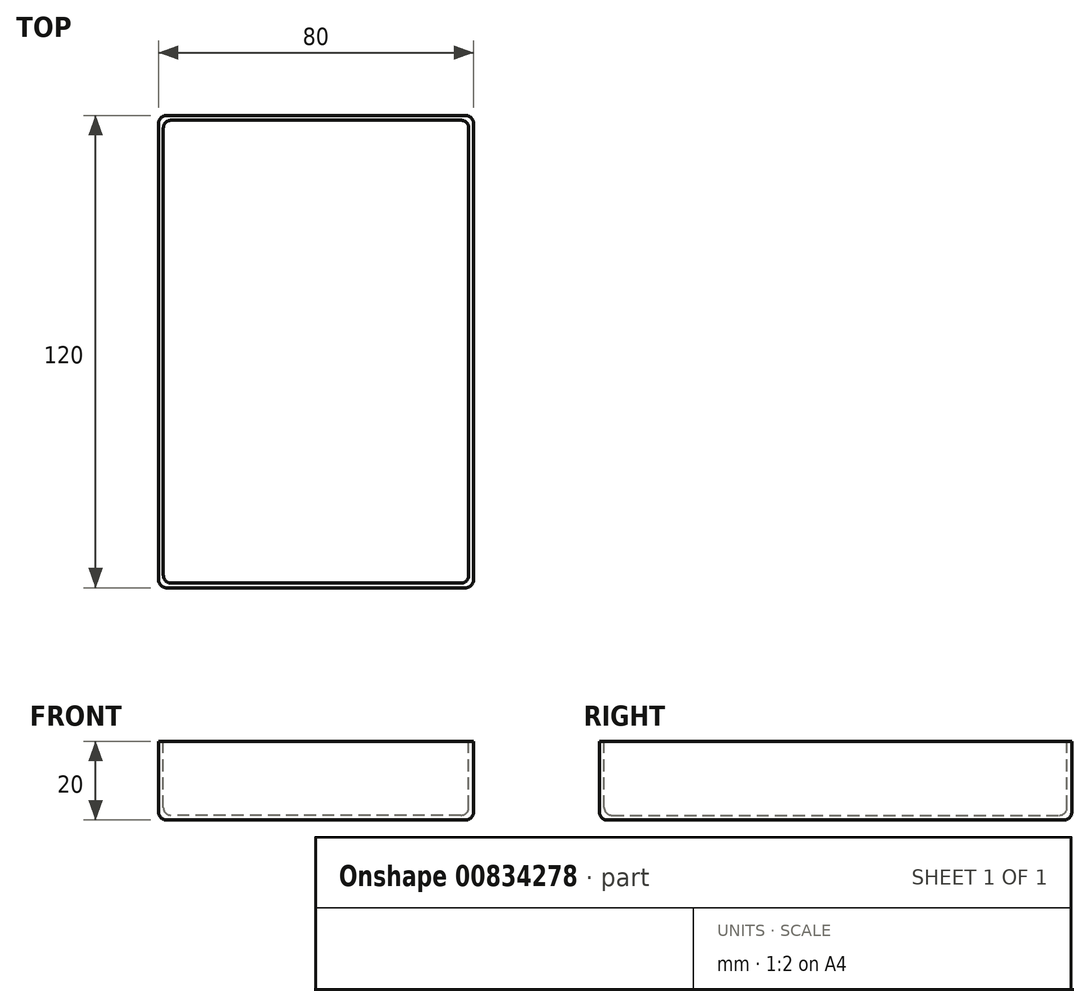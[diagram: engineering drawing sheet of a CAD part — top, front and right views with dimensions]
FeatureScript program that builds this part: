
annotation { "Feature Type Name" : "Feature", "Feature Type Description" : "" }
export const myFeature = defineFeature(function(context is Context, id is Id, definition is map)
    precondition{}
    {
        {
            var Q0;
            Q0=qCreatedBy(makeId("Top.planeOp"),FACE);
            var sketch = newSketch(context, id + "F0", { "sketchPlane" : qUnion([Q0])});
            skLineSegment(sketch, "E0.bottom", {"start": v(-40, -60) * mm, "end": v(40, -60) * mm});
            skLineSegment(sketch, "E0.top", {"start": v(-40, 60) * mm, "end": v(40, 60) * mm});
            skLineSegment(sketch, "E0.left", {"start": v(-40, -60) * mm, "end": v(-40, 60) * mm});
            skLineSegment(sketch, "E0.right", {"start": v(40, -60) * mm, "end": v(40, 60) * mm});
            skPoint(sketch, "E0.middle", {"position": v(0, 0) * mm});
            skSolve(sketch);
        }
        {
            var Q0;
            Q0 = qSketchRegion(id + "F0", true);
            extrude(context, id + "F1", {"entities" : qUnion([Q0]), "depth" : 20 * mm, "offsetDistance" : 25 * mm});
        }
        {
            var Q0;
            Q0=makeQuery(id+"F1.opExtrude","CAP_FACE",FACE,{"disambiguationData":[OSD([sQuery(id+"F0.wireOp",EDGE,"E0.bottom"),sQuery(id+"F0.wireOp",EDGE,"E0.top"),sQuery(id+"F0.wireOp",EDGE,"E0.left"),sQuery(id+"F0.wireOp",EDGE,"E0.right")])],"isStart":false});
            var sketch = newSketch(context, id + "F2", { "sketchPlane" : qUnion([Q0])});
            skLineSegment(sketch, "E1.bottom", {"start": v(38.8, -58.8) * mm, "end": v(-38.8, -58.8) * mm});
            skLineSegment(sketch, "E1.top", {"start": v(38.8, 58.8) * mm, "end": v(-38.8, 58.8) * mm});
            skLineSegment(sketch, "E1.left", {"start": v(38.8, -58.8) * mm, "end": v(38.8, 58.8) * mm});
            skLineSegment(sketch, "E1.right", {"start": v(-38.8, -58.8) * mm, "end": v(-38.8, 58.8) * mm});
            skPoint(sketch, "E1.middle", {"position": v(0, 0) * mm});
            skSolve(sketch);
        }
        {
            var Q0;
            Q0 = qSketchRegion(id + "F2", true);
            extrude(context, id + "F3", {"entities" : qUnion([Q0]), "operationType" : NewBodyOperationType.REMOVE, "oppositeDirection" : true, "depth" : 18.8 * mm, "offsetDistance" : 25 * mm});
        }
        {
            var Q0;
            Q0=makeQuery(id+"F1.opExtrude","SWEPT_EDGE",EDGE,{"disambiguationData":[OSD([sQuery(id+"F0.wireOp",EDGE,"E0.bottom"),sQuery(id+"F0.wireOp",EDGE,"E0.right")])]});
            var Q1;
            Q1=makeQuery(id+"F1.opExtrude","SWEPT_EDGE",EDGE,{"disambiguationData":[OSD([sQuery(id+"F0.wireOp",EDGE,"E0.top"),sQuery(id+"F0.wireOp",EDGE,"E0.right")])]});
            var Q2;
            Q2=makeQuery(id+"F1.opExtrude","SWEPT_EDGE",EDGE,{"disambiguationData":[OSD([sQuery(id+"F0.wireOp",EDGE,"E0.bottom"),sQuery(id+"F0.wireOp",EDGE,"E0.left")])]});
            var Q3;
            Q3=makeQuery(id+"F1.opExtrude","SWEPT_EDGE",EDGE,{"disambiguationData":[OSD([sQuery(id+"F0.wireOp",EDGE,"E0.top"),sQuery(id+"F0.wireOp",EDGE,"E0.left")])]});
            fillet(context, id + "F4", {"entities" : qUnion([Q0, Q1, Q2, Q3]), "radius" : 2 * mm, "tangentPropagation" : true, "allowEdgeOverflow" : false});
        }
        {
            var Q0;
            Q0=makeQuery(id+"F3.boolean.opBoolean","COPY",EDGE,{"derivedFrom":makeQuery(id+"F3.opExtrude","SWEPT_EDGE",EDGE,{"disambiguationData":[OSD([sQuery(id+"F2.wireOp",EDGE,"E1.top"),sQuery(id+"F2.wireOp",EDGE,"E1.right")])]})});
            var Q1;
            Q1=makeQuery(id+"F3.boolean.opBoolean","COPY",EDGE,{"derivedFrom":makeQuery(id+"F3.opExtrude","SWEPT_EDGE",EDGE,{"disambiguationData":[OSD([sQuery(id+"F2.wireOp",EDGE,"E1.bottom"),sQuery(id+"F2.wireOp",EDGE,"E1.right")])]})});
            var Q2;
            Q2=makeQuery(id+"F3.boolean.opBoolean","COPY",EDGE,{"derivedFrom":makeQuery(id+"F3.opExtrude","SWEPT_EDGE",EDGE,{"disambiguationData":[OSD([sQuery(id+"F2.wireOp",EDGE,"E1.bottom"),sQuery(id+"F2.wireOp",EDGE,"E1.left")])]})});
            var Q3;
            Q3=makeQuery(id+"F3.boolean.opBoolean","COPY",EDGE,{"derivedFrom":makeQuery(id+"F3.opExtrude","SWEPT_EDGE",EDGE,{"disambiguationData":[OSD([sQuery(id+"F2.wireOp",EDGE,"E1.top"),sQuery(id+"F2.wireOp",EDGE,"E1.left")])]})});
            fillet(context, id + "F5", {"entities" : qUnion([Q0, Q1, Q2, Q3]), "radius" : 2 * mm, "tangentPropagation" : true, "allowEdgeOverflow" : false});
        }
        {
            var Q0;
            Q0=makeQuery(id+"F3.boolean.opBoolean","COPY",FACE,{"derivedFrom":makeQuery(id+"F3.opExtrude","CAP_FACE",FACE,{"disambiguationData":[OSD([sQuery(id+"F2.wireOp",EDGE,"E1.bottom"),sQuery(id+"F2.wireOp",EDGE,"E1.top"),sQuery(id+"F2.wireOp",EDGE,"E1.left"),sQuery(id+"F2.wireOp",EDGE,"E1.right")])],"isStart":false})});
            fillet(context, id + "F6", {"entities" : qUnion([Q0]), "radius" : 2 * mm, "tangentPropagation" : true, "allowEdgeOverflow" : false});
        }
        {
            var Q0;
            Q0=makeQuery(id+"F1.opExtrude","CAP_FACE",FACE,{"disambiguationData":[OSD([sQuery(id+"F0.wireOp",EDGE,"E0.bottom"),sQuery(id+"F0.wireOp",EDGE,"E0.top"),sQuery(id+"F0.wireOp",EDGE,"E0.left"),sQuery(id+"F0.wireOp",EDGE,"E0.right")])],"isStart":true});
            fillet(context, id + "F7", {"entities" : qUnion([Q0]), "radius" : 2 * mm, "tangentPropagation" : true, "allowEdgeOverflow" : false});
        }
    });
